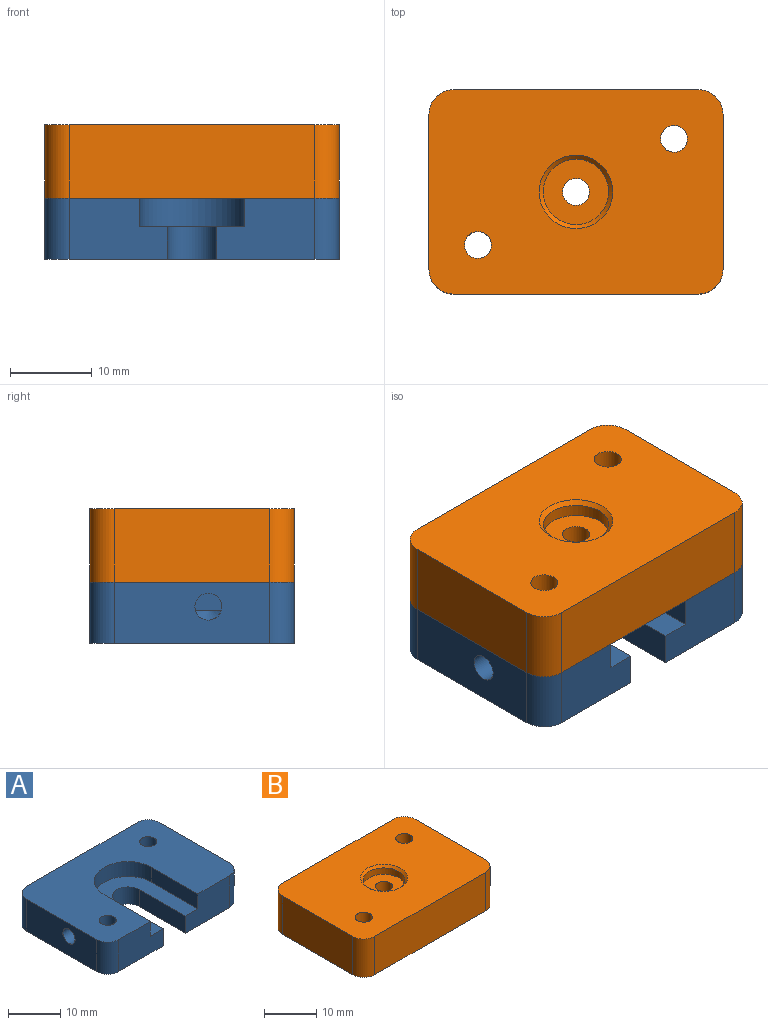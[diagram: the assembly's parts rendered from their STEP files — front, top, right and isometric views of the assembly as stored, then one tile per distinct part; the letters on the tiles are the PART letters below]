
ASSEMBLY  parts=2 mates=1
PART A: 26 faces, bbox 36x25x7.5 mm
  f0: plane 8.25x7.05mm, normal (0,0,-1), area 40.1mm2, adj f1,f14,f25
  f1: cylinder r=4.12mm len=8.25mm, axis (0,0,-1), area 98mm2, adj f0,f4,f25
  f2: plane 18.95x12.9mm, normal (0,0,1), area 135.7mm2, adj f3,f5,f18,f19,f20,f21,f22,f23
  f3: plane 12x7.5mm, normal (0,-1,0), area 77.9mm2, adj f2,f4,f8,f13,f20,f23
  f4: plane 36x25mm, normal (0,0,-1), area 696.2mm2, adj f1,f3,f5,f6,f7,f9,f10,f11
  f5: plane 12x7.5mm, normal (0,-1,0), area 77.9mm2, adj f2,f4,f8,f12,f19,f21
  f6: plane 19x7.5mm, normal (-1,0,0), area 133.9mm2, adj f4,f8,f11,f13,f25
  f7: plane 19x7.5mm, normal (1,0,0), area 142.5mm2, adj f4,f8,f10,f12
  f8: plane 36x25mm, normal (0,0,1), area 648.6mm2, adj f3,f5,f6,f7,f9,f10,f11,f12
  f9: plane 30x7.5mm, normal (0,1,0), area 225mm2, adj f4,f8,f10,f11
  f10: cylinder r=3mm len=7.5mm, axis (0,0,1), area 35.3mm2, adj f4,f7,f8,f9
  f11: cylinder r=3mm len=7.5mm, axis (0,0,-1), area 35.3mm2, adj f4,f6,f8,f9
  f12: cylinder r=3mm len=7.5mm, axis (0,0,-1), area 35.3mm2, adj f4,f5,f7,f8
  f13: cylinder r=3mm len=7.5mm, axis (0,0,1), area 35.3mm2, adj f3,f4,f6,f8
  f14: cylinder r=1.65mm len=3.5mm, axis (0,0,-1), area 36.3mm2, adj f0,f8
  f15: cylinder r=1.65mm len=3.5mm, axis (0,0,-1), area 36.3mm2, adj f8,f16
  f16: plane 8.25x8.25mm, normal (0,0,-1), area 44.9mm2, adj f15,f17
  f17: cylinder r=4.12mm len=8.25mm, axis (0,0,-1), area 103.7mm2, adj f4,f16
  f18: cylinder r=3mm len=6mm, axis (0,0,-1), area 37.7mm2, adj f2,f4,f19,f20
  f19: plane 12.5x4mm, normal (-1,0,0), area 50mm2, adj f2,f4,f5,f18
  f20: plane 12.5x4mm, normal (1,0,0), area 50mm2, adj f2,f3,f4,f18
  f21: plane 12.5x3.5mm, normal (-1,0,0), area 43.8mm2, adj f2,f5,f8,f22
  f22: cylinder r=6.45mm len=12.9mm, axis (0,0,1), area 70.9mm2, adj f2,f8,f21,f23
  f23: plane 12.5x3.5mm, normal (1,0,0), area 37.8mm2, adj f2,f3,f8,f22,f25
  f24: cone r=0mm half-angle=59deg, axis (-1,0,0), area 3.1mm2, adj f2,f25
  f25: cylinder r=1.65mm len=11.7mm, axis (-1,0,0), area 113mm2, adj f0,f1,f2,f6,f23,f24
PART B: 18 faces, bbox 36x25x9 mm
  f0: cylinder r=1.65mm len=3.3mm, axis (0,0,-1), area 31.1mm2, adj f11,f16
  f1: plane 19x9mm, normal (-1,0,0), area 171mm2, adj f2,f4,f8,f10
  f2: plane 36x25mm, normal (0,0,-1), area 821.7mm2, adj f1,f3,f5,f6,f7,f8,f9,f10
  f3: plane 19x9mm, normal (1,0,0), area 171mm2, adj f2,f4,f7,f9
  f4: plane 36x25mm, normal (0,0,1), area 811.6mm2, adj f1,f3,f5,f6,f7,f8,f9,f10
  f5: plane 30x9mm, normal (0,-1,0), area 270mm2, adj f2,f4,f9,f10
  f6: plane 30x9mm, normal (0,1,0), area 270mm2, adj f2,f4,f7,f8
  f7: cylinder r=3mm len=9mm, axis (0,0,1), area 42.4mm2, adj f2,f3,f4,f6
  f8: cylinder r=3mm len=9mm, axis (0,0,-1), area 42.4mm2, adj f1,f2,f4,f6
  f9: cylinder r=3mm len=9mm, axis (0,0,-1), area 42.4mm2, adj f2,f3,f4,f5
  f10: cylinder r=3mm len=9mm, axis (0,0,1), area 42.4mm2, adj f1,f2,f4,f5
  f11: plane 8.25x8.25mm, normal (0,0,-1), area 44.9mm2, adj f0,f12
  f12: cylinder r=4.12mm len=8.25mm, axis (0,0,-1), area 103.7mm2, adj f2,f11
  f13: cylinder r=1.65mm len=9mm, axis (0,0,-1), area 93.3mm2, adj f2,f4
  f14: cylinder r=1.65mm len=9mm, axis (0,0,-1), area 93.3mm2, adj f2,f4
  f15: cylinder r=4mm len=8mm, axis (0,0,1), area 37.7mm2, adj f16,f17
  f16: plane 8x8mm, normal (0,0,1), area 41.7mm2, adj f0,f15
  f17: cone r=4mm half-angle=45deg, axis (0,0,1), area 18.9mm2, adj f4,f15
PLACE A t=(-5.23,-35.35,49.69)mm
PLACE B t=(-5.23,-35.35,57.19)mm
MATE fastened A.f1 <-> B.f14  axis (0,0,1) through (-17.23,-54.35,57.19)mm
